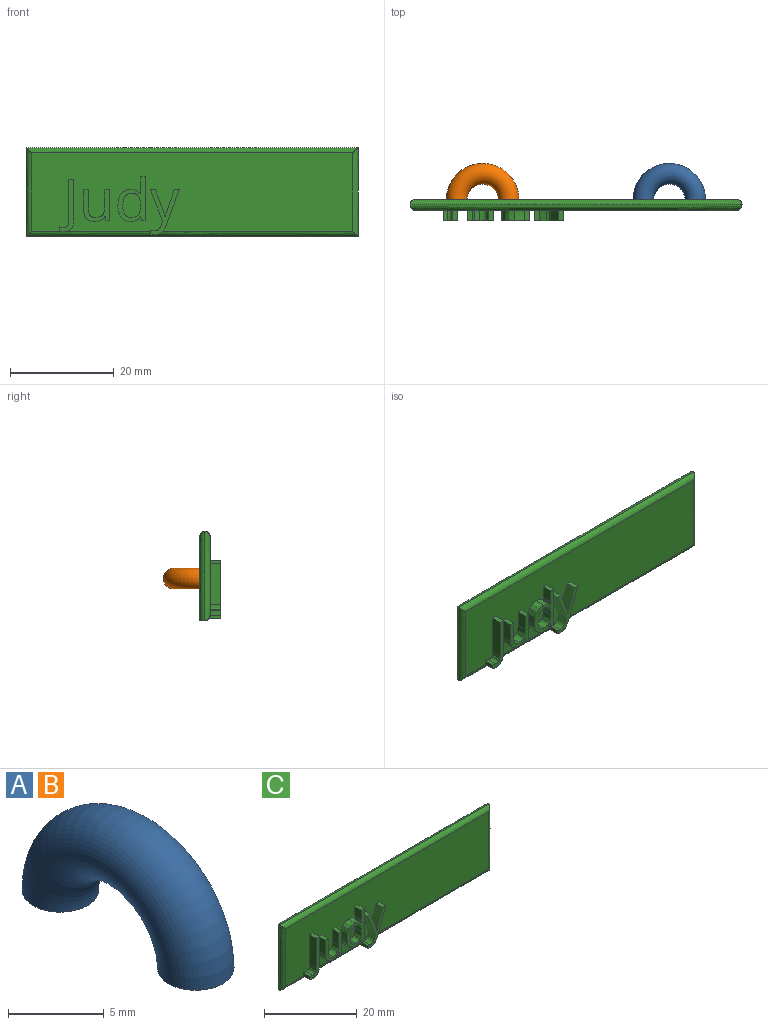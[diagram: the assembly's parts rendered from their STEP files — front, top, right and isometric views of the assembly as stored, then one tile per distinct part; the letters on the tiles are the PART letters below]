
ASSEMBLY  parts=3 mates=2
PART A: 3 faces, bbox 4x15.2x7.6 mm
  f0: torus R=5mm, axis (-1,0,0), area 197.4mm2, adj f1,f2
  f1: plane 4x4mm, normal (0,0,-1), area 12.6mm2, adj f0
  f2: plane 4x4mm, normal (0,0,-1), area 12.6mm2, adj f0
PART B: same geometry as A
PART C: 82 faces, bbox 68.6x4.1x18.9 mm
  f0: plane 61.94x15.17mm, normal (0,-1,0), area 870.8mm2, adj f3,f4,f5,f6,f7,f8,f9,f10
  f1: plane 64.03x1.09mm, normal (0,0,-1), area 63.4mm2, adj f2,f76,f78,f81
  f2: plane 61.94x16.14mm, normal (0,1,0), area 999.5mm2, adj f1,f78,f80,f81
  f3: extruded ~2x0.81mm, area 1.7mm2, adj f0,f4,f12,f13,f76
  f4: extruded ~2x1.51mm, area 3.3mm2, adj f0,f3,f5,f13,f76
  f5: extruded ~2x1.61mm, area 3.5mm2, adj f0,f4,f6,f13
  f6: plane 7.9x2mm, normal (1,0,0), area 15.8mm2, adj f0,f5,f7,f13
  f7: plane 2x0.93mm, normal (0,0,1), area 1.9mm2, adj f0,f6,f8,f13
  f8: plane 7.98x2mm, normal (-1,0,0), area 16mm2, adj f0,f7,f9,f13
  f9: extruded ~2x0.94mm, area 2mm2, adj f0,f8,f10,f13
  f10: extruded ~2x0.82mm, area 1.8mm2, adj f0,f9,f11,f13
  f11: extruded ~2x0.81mm, area 1.6mm2, adj f0,f10,f12,f13
  f12: plane 2x0.79mm, normal (-1,0,0), area 1.6mm2, adj f0,f3,f11,f13
  f13: plane 10.08x2.84mm, normal (0,-1,0), area 10.4mm2, adj f3,f4,f5,f6,f7,f8,f9,f10
  f14: plane 3.88x2mm, normal (1,0,0), area 7.8mm2, adj f0,f15,f30,f31
  f15: plane 2x0.92mm, normal (0,0,1), area 1.8mm2, adj f0,f14,f16,f31
  f16: plane 3.91x2mm, normal (-1,0,0), area 7.8mm2, adj f0,f15,f17,f31
  f17: extruded ~2x1.66mm, area 3.6mm2, adj f0,f16,f18,f31
  f18: extruded ~2x1.63mm, area 3.5mm2, adj f0,f17,f19,f31
  f19: extruded ~2x1.13mm, area 2.3mm2, adj f0,f18,f20,f31
  f20: extruded ~2x0.77mm, area 2.1mm2, adj f0,f19,f21,f31
  f21: plane 2x0.05mm, normal (0,0,-1), area 0.1mm2, adj f0,f20,f22,f31
  f22: plane 2x0.8mm, normal (-0.99,0,-0.16), area 1.6mm2, adj f0,f21,f23,f31
  f23: plane 2x0.75mm, normal (0,0,-1), area 1.5mm2, adj f0,f22,f24,f31
  f24: plane 5.98x2mm, normal (1,0,0), area 12mm2, adj f0,f23,f25,f31
  f25: plane 2x0.91mm, normal (0,0,1), area 1.8mm2, adj f0,f24,f26,f31
  f26: plane 3.14x2mm, normal (-1,0,0), area 6.3mm2, adj f0,f25,f27,f31
  f27: extruded ~2x1.68mm, area 3.5mm2, adj f0,f26,f28,f31
  f28: extruded ~2x1.37mm, area 3mm2, adj f0,f27,f29,f31
  f29: extruded ~2x1.04mm, area 2.3mm2, adj f0,f28,f30,f31
  f30: extruded ~2x1.09mm, area 2.3mm2, adj f0,f14,f29,f31
  f31: plane 6.09x5mm, normal (0,-1,0), area 13mm2, adj f14,f15,f16,f17,f18,f19,f20,f21
  f32: extruded ~2x1.34mm, area 3mm2, adj f33,f55,f56,f57
  f33: extruded ~2x1.23mm, area 2.8mm2, adj f32,f34,f56,f57
  f34: extruded ~2x1.73mm, area 3.6mm2, adj f33,f35,f56,f57
  f35: extruded ~2x1.75mm, area 3.6mm2, adj f34,f36,f56,f57
  f36: extruded ~2x1.22mm, area 2.9mm2, adj f35,f37,f56,f57
  f37: extruded ~2x1.35mm, area 3mm2, adj f36,f38,f56,f57
  f38: extruded ~2x1.81mm, area 3.8mm2, adj f37,f39,f56,f57
  f39: plane 2x0.19mm, normal (-1,0,0), area 0.4mm2, adj f38,f55,f56,f57
  f40: plane 2x0.05mm, normal (0,0,-1), area 0.1mm2, adj f0,f41,f54,f56
  f41: plane 2x0.8mm, normal (-0.99,0,-0.15), area 1.6mm2, adj f0,f40,f42,f56
  f42: plane 2x0.74mm, normal (0,0,-1), area 1.5mm2, adj f0,f41,f43,f56
  f43: plane 8.49x2mm, normal (1,0,0), area 17mm2, adj f0,f42,f44,f56
  f44: plane 2x0.91mm, normal (0,0,1), area 1.8mm2, adj f0,f43,f45,f56
  f45: plane 2.43x2mm, normal (-1,0,0), area 4.9mm2, adj f0,f44,f46,f56
  f46: plane 2x0.42mm, normal (-1,0,-0.05), area 0.8mm2, adj f0,f45,f47,f56
  f47: plane 2x0.43mm, normal (-1,0,-0.09), area 0.9mm2, adj f0,f46,f48,f56
  f48: plane 2x0.07mm, normal (0,0,1), area 0.1mm2, adj f0,f47,f49,f56
  f49: extruded ~2x1.87mm, area 4.3mm2, adj f0,f48,f50,f56
  f50: extruded ~2x1.82mm, area 4.1mm2, adj f0,f49,f51,f56
  f51: extruded ~2.3x2mm, area 4.9mm2, adj f0,f50,f52,f56
  f52: extruded ~2.28x2mm, area 4.8mm2, adj f0,f51,f53,f56
  f53: extruded ~2x1.83mm, area 4.1mm2, adj f0,f52,f54,f56
  f54: extruded ~2x1.88mm, area 4.4mm2, adj f0,f40,f53,f56
  f55: extruded ~2x1.63mm, area 3.4mm2, adj f32,f39,f56,f57
  f56: plane 8.6x5.26mm, normal (0,-1,0), area 17.4mm2, adj f32,f33,f34,f35,f36,f37,f38,f39
  f57: plane 4.68x3.41mm, normal (0,-1,0), area 13.4mm2, adj f32,f33,f34,f35,f36,f37,f38,f39
  f58: plane 2x0.97mm, normal (0,0,1), area 1.9mm2, adj f0,f59,f73,f74
  f59: plane 6.01x2.41mm, normal (-0.93,0,-0.37), area 13mm2, adj f0,f58,f60,f74
  f60: plane 2x0.85mm, normal (-0.93,0,0.37), area 1.8mm2, adj f0,f59,f61,f74
  f61: extruded ~2x1.33mm, area 3.6mm2, adj f0,f60,f62,f74
  f62: extruded ~2x0.67mm, area 1.3mm2, adj f0,f61,f63,f74
  f63: plane 2.28x0.8mm, normal (-1,0,0), area 1.5mm2, adj f0,f62,f64,f74,f76
  f64: extruded ~2.29x0.82mm, area 1.9mm2, adj f63,f65,f74,f76
  f65: extruded ~2.29x1.25mm, area 2.9mm2, adj f64,f66,f74,f76
  f66: extruded ~2.03x1.43mm, area 3.4mm2, adj f0,f65,f67,f74,f76
  f67: plane 6.81x2.57mm, normal (0.94,0,-0.35), area 14.6mm2, adj f0,f66,f68,f74
  f68: plane 2x0.97mm, normal (0,0,1), area 1.9mm2, adj f0,f67,f69,f74
  f69: extruded ~4.14x2mm, area 8.8mm2, adj f0,f68,f70,f74
  f70: extruded ~2x0.95mm, area 2mm2, adj f0,f69,f71,f74
  f71: plane 2x0.04mm, normal (0,0,1), area 0.1mm2, adj f0,f70,f72,f74
  f72: extruded ~2x1.69mm, area 3.5mm2, adj f0,f71,f73,f74
  f73: plane 3.41x2mm, normal (0.93,0,0.36), area 7.3mm2, adj f0,f58,f72,f74
  f74: plane 8.66x5.61mm, normal (0,-1,0), area 13.9mm2, adj f58,f59,f60,f61,f62,f63,f64,f65
  f75: bspline ~18.85x1mm, area 25.3mm2, adj f0,f76,f77,f78
  f76: bspline ~68.47x1mm, area 97.7mm2, adj f0,f1,f3,f4,f63,f64,f65,f66
  f77: bspline ~68.47x1mm, area 98.6mm2, adj f0,f75,f79,f80
  f78: bspline ~18.85x1mm, area 26.1mm2, adj f1,f2,f75,f80
  f79: bspline ~18.85x1mm, area 25.3mm2, adj f0,f76,f77,f81
  f80: bspline ~68.47x1mm, area 98.6mm2, adj f2,f77,f78,f81
  f81: bspline ~18.85x1mm, area 26.1mm2, adj f1,f2,f79,f80
PLACE A rot(axis=(-0.58,0.58,0.58),120deg) t=(30.53,8.83,3.02)mm
PLACE B rot(axis=(-0.58,0.58,0.58),120deg) t=(-5.41,8.83,3.02)mm
PLACE C t=(3.39,1.83,-2.05)mm
MATE fastened B.f2 <-> C.f2  axis (0,-1,0) through (-10.41,3.83,3.02)mm
MATE fastened A.f1 <-> C.f2  axis (0,-1,0) through (35.53,3.83,3.02)mm
